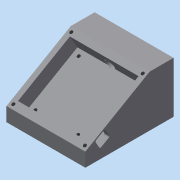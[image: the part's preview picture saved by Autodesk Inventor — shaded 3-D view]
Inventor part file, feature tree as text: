
AUTODESK INVENTOR PART (.ipt)
format: ipt  version: 2018 (Build 220112000, 112)  size: 173,056 bytes
history: native  units: mm
features: reference x8, sketch x7, extrude x4, other x4, fillet x3, hole x3, projected_geometry x1
ambient origin geometry x8: Origin, YZ Plane, XZ Plane, XY Plane, X Axis, Y Axis, Z Axis, Center Point
bodies: Volumenkörper1 (feature_tree)
feature tree (30):
  extrude  "Extrusion1"  Depth=95.0mm
  extrude  "Extrusion2"  Depth=15.0mm
  extrude  "Extrusion3"  TaperAngle=120.0deg  [1 undecoded]
  extrude  "Extrusion4"  Depth=74.0mm
  fillet  "Rundung2"  Radius=64.5mm
  hole  "Bohrung2"  [1 undecoded]
  hole  "Bohrung3"  [1 undecoded]
  hole  "Bohrung4"  [1 undecoded]
  fillet  "Rundung3"  Radius=10.8mm
  fillet  "Rundung1"  Radius=1.46mm
  sketch  "Skizze1"  dims[d0=85.0mm d1=95.0mm]
  sketch  "Skizze2"  dims[d2=80.0mm d3=0.0mm d4=15.0mm]
  sketch  "Skizze3"  dims[d5=80.0mm d6=120.0deg]
  sketch  "Skizze4"  dims[d7=80.0mm d8=0.0mm d9=74.0mm d10=64.5mm]
  sketch  "Skizze6"  dims[d11=16.36mm d12=0.0mm d13=8.0mm]
  reference  "Referenz5"
  reference  "Referenz6"
  reference  "Referenz7"
  reference  "Referenz8"
  sketch  "Skizze7"  dims[d14=3.1mm d15=4.1mm]
  projected_geometry  "Projizierte Kontur1"
  sketch  "Skizze8"  dims[d16=3.15mm d17=12.2mm d18=10.8mm d19=1.46mm d20=20.0mm d21=0.0mm d22=1.5mm d30=3.242mm d31=8.0mm d32=4.0mm d33=2.0mm d34=90.0deg d35=11.8mm d36=20.594885mm d37=42.5mm d38=14.0mm d39=10.0mm d40=8.0mm d41=4.0mm d42=2.0mm d43=90.0deg d44=11.8mm d45=20.594885mm d46=1.5mm d47=2.459mm d48=6.0mm d49=4.0mm d50=2.0mm d51=90.0deg d52=7.0mm d53=20.594885mm]
  reference  "Referenz9"
  reference  "Referenz11"
  reference  "Referenz12"
  reference  "Referenz13"
  other  "<userpath>\Documents\Waage\CAD\Main.iam"
  other  "Main.iam"
  other  "Schiled:1"
  other  "WaagePCB:1"
note: 4 required parameter values undecoded (feature->parameter linkage not recoverable at this tier; creation-order binding heuristic only, values carry confidence <= 0.55)
